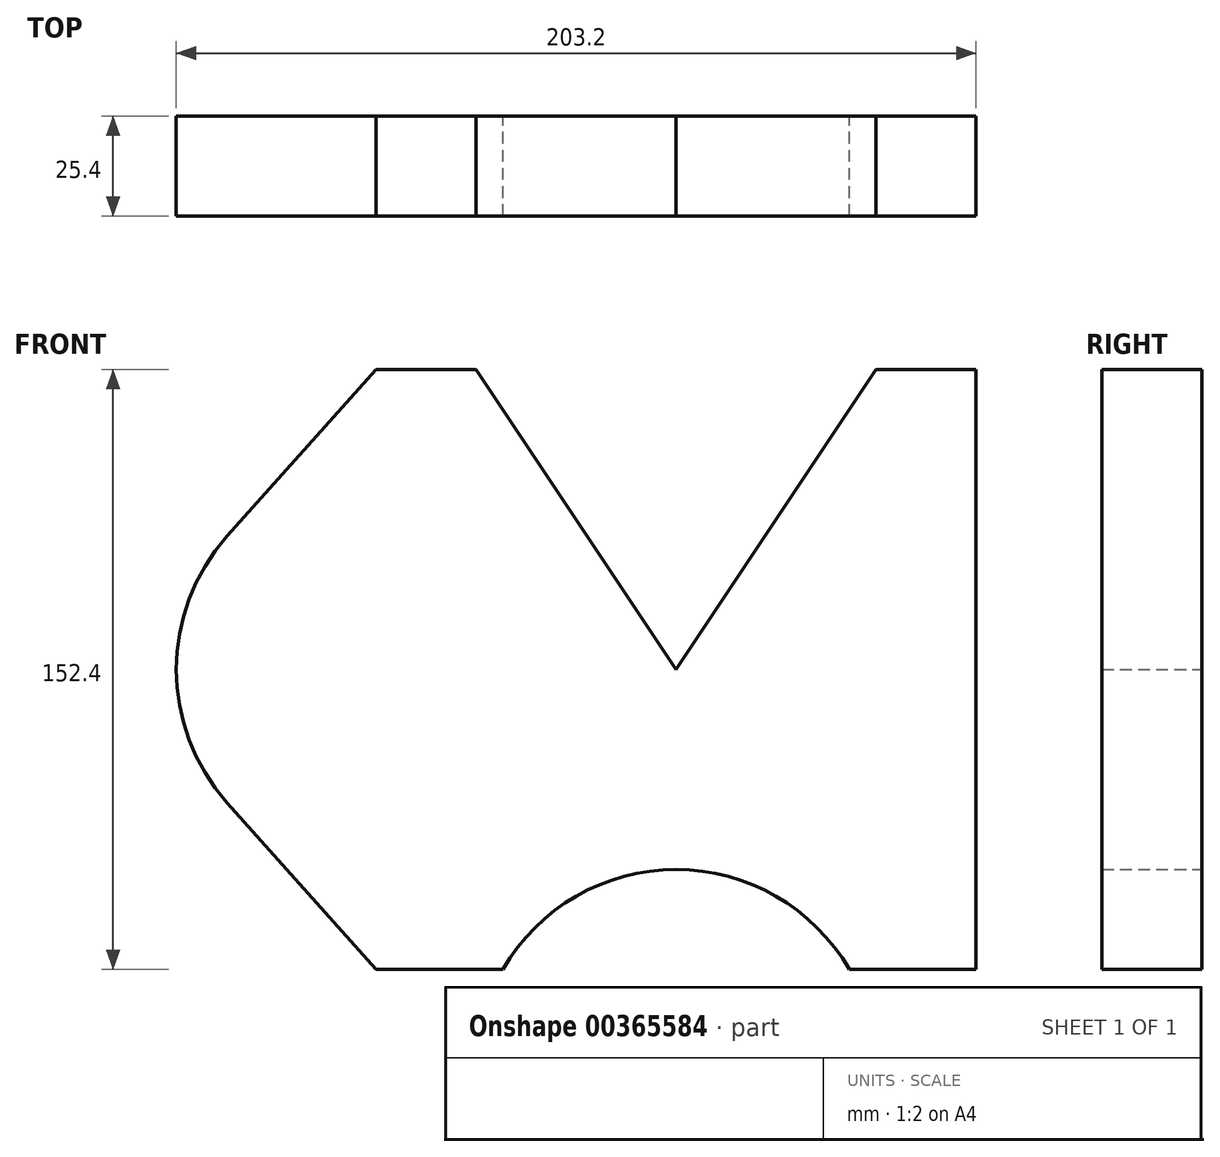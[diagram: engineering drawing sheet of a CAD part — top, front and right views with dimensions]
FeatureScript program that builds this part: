
annotation { "Feature Type Name" : "Feature", "Feature Type Description" : "" }
export const myFeature = defineFeature(function(context is Context, id is Id, definition is map)
    precondition{}
    {
        {
            var Q0;
            Q0=qCreatedBy(makeId("Front.planeOp"),FACE);
            var sketch = newSketch(context, id + "F0", { "sketchPlane" : qUnion([Q0])});
            skLineSegment(sketch, "E0", {"start": v(-76.2, 76.2) * mm, "end": v(-50.8, 76.2) * mm});
            skLineSegment(sketch, "E1", {"start": v(-50.8, 76.2) * mm, "end": v(0, 0) * mm});
            skLineSegment(sketch, "E2", {"start": v(0, 0) * mm, "end": v(50.8, 76.2) * mm});
            skLineSegment(sketch, "E3", {"start": v(50.8, 76.2) * mm, "end": v(76.2, 76.2) * mm});
            skLineSegment(sketch, "E4", {"start": v(76.2, 76.2) * mm, "end": v(76.2, -76.2) * mm});
            skLineSegment(sketch, "E5", {"start": v(76.2, -76.2) * mm, "end": v(44, -76.2) * mm});
            skLineSegment(sketch, "E6", {"start": v(-44, -76.2) * mm, "end": v(-76.2, -76.2) * mm});
            skLineSegment(sketch, "E7", {"start": v(-76.2, -76.2) * mm, "end": v(-114.06, -33.87) * mm});
            skArc(sketch, "E8", {"start": v(-114.06, -33.87) * mm, "mid": v(-127, 0) * mm, "end": v(-114.06, 33.87) * mm});
            skLineSegment(sketch, "E9", {"start": v(-114.06, 33.87) * mm, "end": v(-76.2, 76.2) * mm});
            skArc(sketch, "E10", {"start": v(-44, -76.2) * mm, "mid": v(0, -50.8) * mm, "end": v(44, -76.2) * mm});
            skLineSegment(sketch, "E11", {"start": v(-76.2, 76.2) * mm, "end": v(-76.2, -87.67) * mm, "construction": true});
            skSolve(sketch);
        }
        {
            var Q0;
            Q0 = qSketchRegion(id + "F0", true);
            extrude(context, id + "F1", {"entities" : qUnion([Q0]), "depth" : 25.4 * mm, "offsetDistance" : 25.4 * mm});
        }
    });
